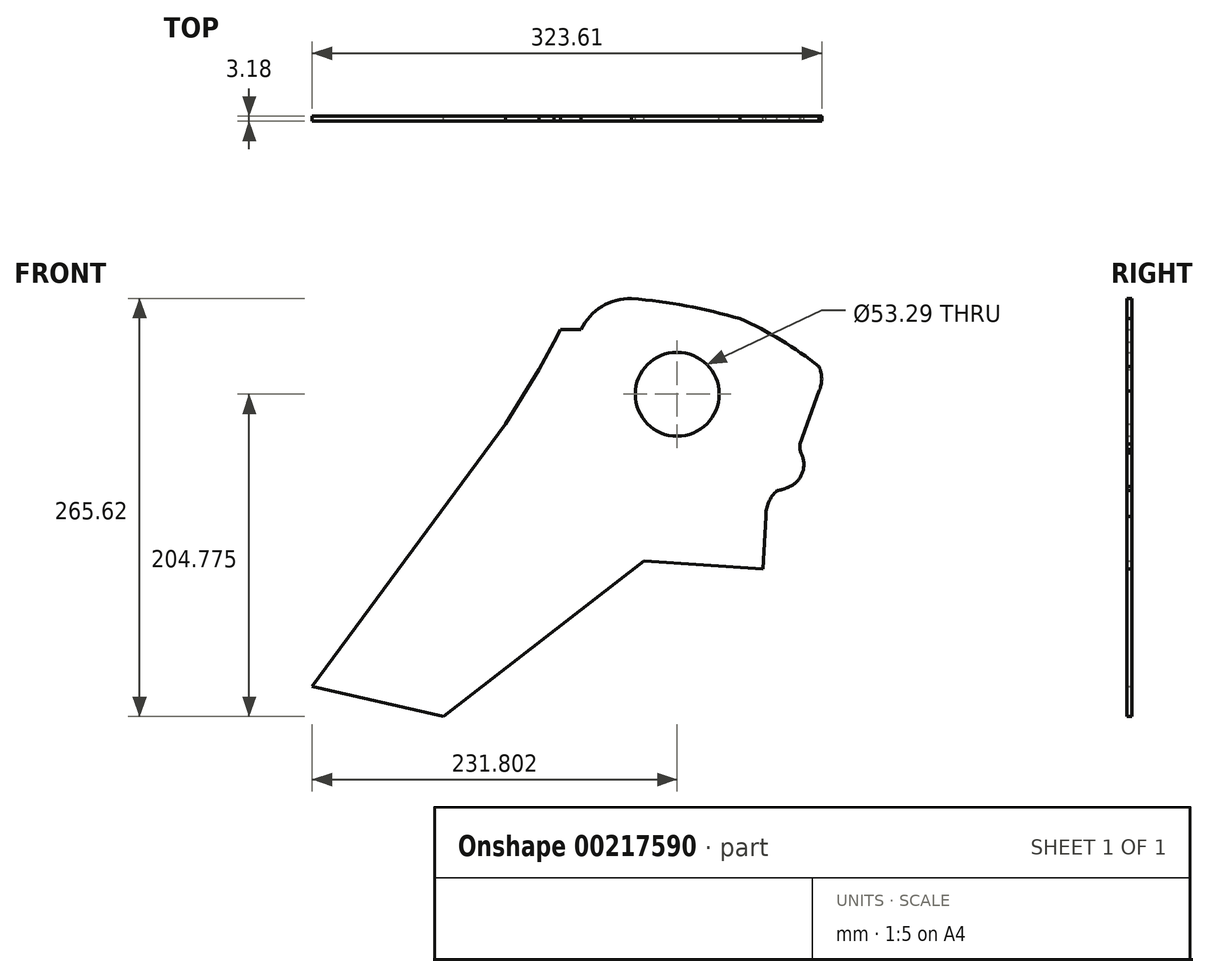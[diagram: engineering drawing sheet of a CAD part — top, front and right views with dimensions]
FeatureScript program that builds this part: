
annotation { "Feature Type Name" : "Feature", "Feature Type Description" : "" }
export const myFeature = defineFeature(function(context is Context, id is Id, definition is map)
    precondition{}
    {
        {
            var Q0;
            Q0=qCreatedBy(makeId("Front.planeOp"),FACE);
            var sketch = newSketch(context, id + "F0", { "sketchPlane" : qUnion([Q0])});
            skLineSegment(sketch, "E0", {"start": v(10.63, -49.38) * mm, "end": v(-72.77, -30.09) * mm});
            skLineSegment(sketch, "E1", {"start": v(10.63, -49.38) * mm, "end": v(138.07, 49.48) * mm});
            skLineSegment(sketch, "E2", {"start": v(138.07, 49.48) * mm, "end": v(213.63, 44.29) * mm});
            skLineSegment(sketch, "E3", {"start": v(213.63, 44.29) * mm, "end": v(215.43, 77.63) * mm});
            skLineSegment(sketch, "E4", {"start": v(-72.77, -30.09) * mm, "end": v(50.12, 136.58) * mm});
            skLineSegment(sketch, "E5", {"start": v(50.12, 136.58) * mm, "end": v(71.14, 171.15) * mm});
            skLineSegment(sketch, "E6", {"start": v(71.14, 171.15) * mm, "end": v(80.82, 188.4) * mm});
            skLineSegment(sketch, "E7", {"start": v(80.82, 188.4) * mm, "end": v(84.9, 196.56) * mm});
            skLineSegment(sketch, "E8", {"start": v(84.9, 196.56) * mm, "end": v(97.95, 196.56) * mm});
            skArc(sketch, "E9", {"start": v(130.15, 216.24) * mm, "mid": v(111.2, 211.07) * mm, "end": v(97.95, 196.56) * mm});
            skArc(sketch, "E10", {"start": v(199.05, 203.36) * mm, "mid": v(164.91, 211.46) * mm, "end": v(130.15, 216.24) * mm});
            skArc(sketch, "E11", {"start": v(249.13, 172.87) * mm, "mid": v(225.07, 189.74) * mm, "end": v(199.05, 203.36) * mm});
            skArc(sketch, "E12", {"start": v(249.13, 157.28) * mm, "mid": v(250.84, 165.08) * mm, "end": v(249.13, 172.87) * mm});
            skLineSegment(sketch, "E13", {"start": v(249.13, 157.28) * mm, "end": v(237.05, 123.65) * mm});
            skLineSegment(sketch, "E14", {"start": v(237.05, 123.65) * mm, "end": v(237.05, 120.38) * mm});
            skLineSegment(sketch, "E15", {"start": v(237.05, 120.38) * mm, "end": v(237.55, 118.11) * mm});
            skArc(sketch, "E16", {"start": v(230.48, 96.72) * mm, "mid": v(238.7, 105.87) * mm, "end": v(237.55, 118.11) * mm});
            skArc(sketch, "E17", {"start": v(222.5, 94.18) * mm, "mid": v(226.59, 95.15) * mm, "end": v(230.48, 96.72) * mm});
            skArc(sketch, "E18", {"start": v(222.5, 94.18) * mm, "mid": v(217.1, 86.7) * mm, "end": v(215.43, 77.63) * mm});
            skCircle(sketch, "E19", {"center": v(159.03, 155.4) * mm, "radius": 26.64 * mm});
            skSolve(sketch);
        }
        {
            var Q0;
            Q0 = qSketchRegion(id + "F0", true);
            extrude(context, id + "F1", {"entities" : qUnion([Q0]), "depth" : 3.17 * mm});
        }
    });
